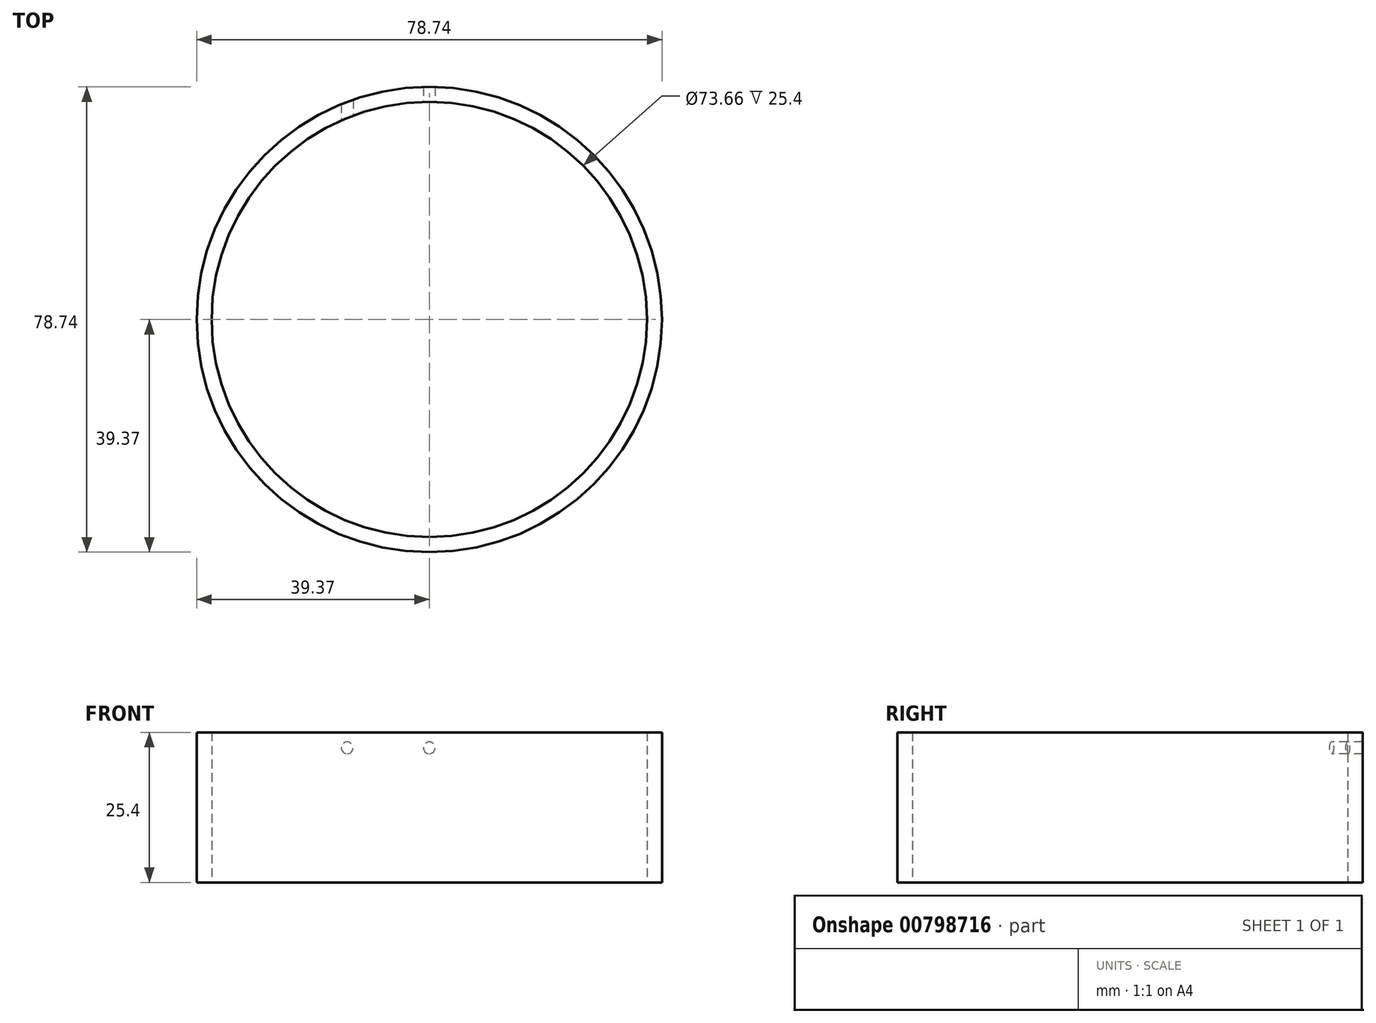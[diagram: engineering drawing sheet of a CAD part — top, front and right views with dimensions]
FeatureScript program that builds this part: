
annotation { "Feature Type Name" : "Feature", "Feature Type Description" : "" }
export const myFeature = defineFeature(function(context is Context, id is Id, definition is map)
    precondition{}
    {
        {
            var Q0;
            Q0=qCreatedBy(makeId("Top.planeOp"),FACE);
            var sketch = newSketch(context, id + "F0", { "sketchPlane" : qUnion([Q0])});
            skCircle(sketch, "E0", {"center": v(0, 0) * mm, "radius": 39.37 * mm});
            skCircle(sketch, "E1.0", {"center": v(0, 0) * mm, "radius": 36.83 * mm});
            skSolve(sketch);
        }
        {
            var Q0;
            Q0=makeQuery(id+"F0.imprint","IMPRINT",FACE,{"disambiguationData":[TD([[makeQuery(id+"F0.imprint","IMPRINT",EDGE,{"derivedFrom":sQuery(id+"F0.wireOp",EDGE,"E0")}),1.0]])]});
            extrude(context, id + "F1", {"entities" : qUnion([Q0]), "depth" : 25.4 * mm, "offsetDistance" : 25.4 * mm});
        }
        {
            var Q0;
            Q0=qCreatedBy(makeId("Front.planeOp"),FACE);
            var sketch = newSketch(context, id + "F2", { "sketchPlane" : qUnion([Q0])});
            skCircle(sketch, "E2", {"center": v(0, 22.77) * mm, "radius": 1 * mm});
            skCircle(sketch, "E3", {"center": v(-13.89, 22.77) * mm, "radius": 1 * mm});
            skLineSegment(sketch, "E4", {"start": v(0, 0) * mm, "end": v(0, 22.77) * mm, "construction": true});
            skLineSegment(sketch, "E5", {"start": v(0, 22.77) * mm, "end": v(-13.89, 22.77) * mm, "construction": true});
            skSolve(sketch);
        }
        {
            var Q0;
            Q0=makeQuery(id+"F2.imprint","IMPRINT",FACE,{"disambiguationData":[TD([[makeQuery(id+"F2.imprint","IMPRINT",EDGE,{"derivedFrom":sQuery(id+"F2.wireOp",EDGE,"E3")}),1.0]])]});
            var Q1;
            Q1=makeQuery(id+"F2.imprint","IMPRINT",FACE,{"disambiguationData":[TD([[makeQuery(id+"F2.imprint","IMPRINT",EDGE,{"derivedFrom":sQuery(id+"F2.wireOp",EDGE,"E2")}),1.0]])]});
            var Q2;
            Q2=sQuery(id+"F2.wireOp",EDGE,"E3");
            var Q3;
            Q3=sQuery(id+"F2.wireOp",EDGE,"E2");
            extrude(context, id + "F3", {"entities" : qUnion([Q0, Q1]), "operationType" : NewBodyOperationType.REMOVE, "surfaceOperationType" : NewSurfaceOperationType.ADD, "surfaceEntities" : qUnion([Q2, Q3]), "endBound" : BoundingType.THROUGH_ALL, "oppositeDirection" : true, "depth" : 25.4 * mm, "offsetDistance" : 25.4 * mm});
        }
    });
